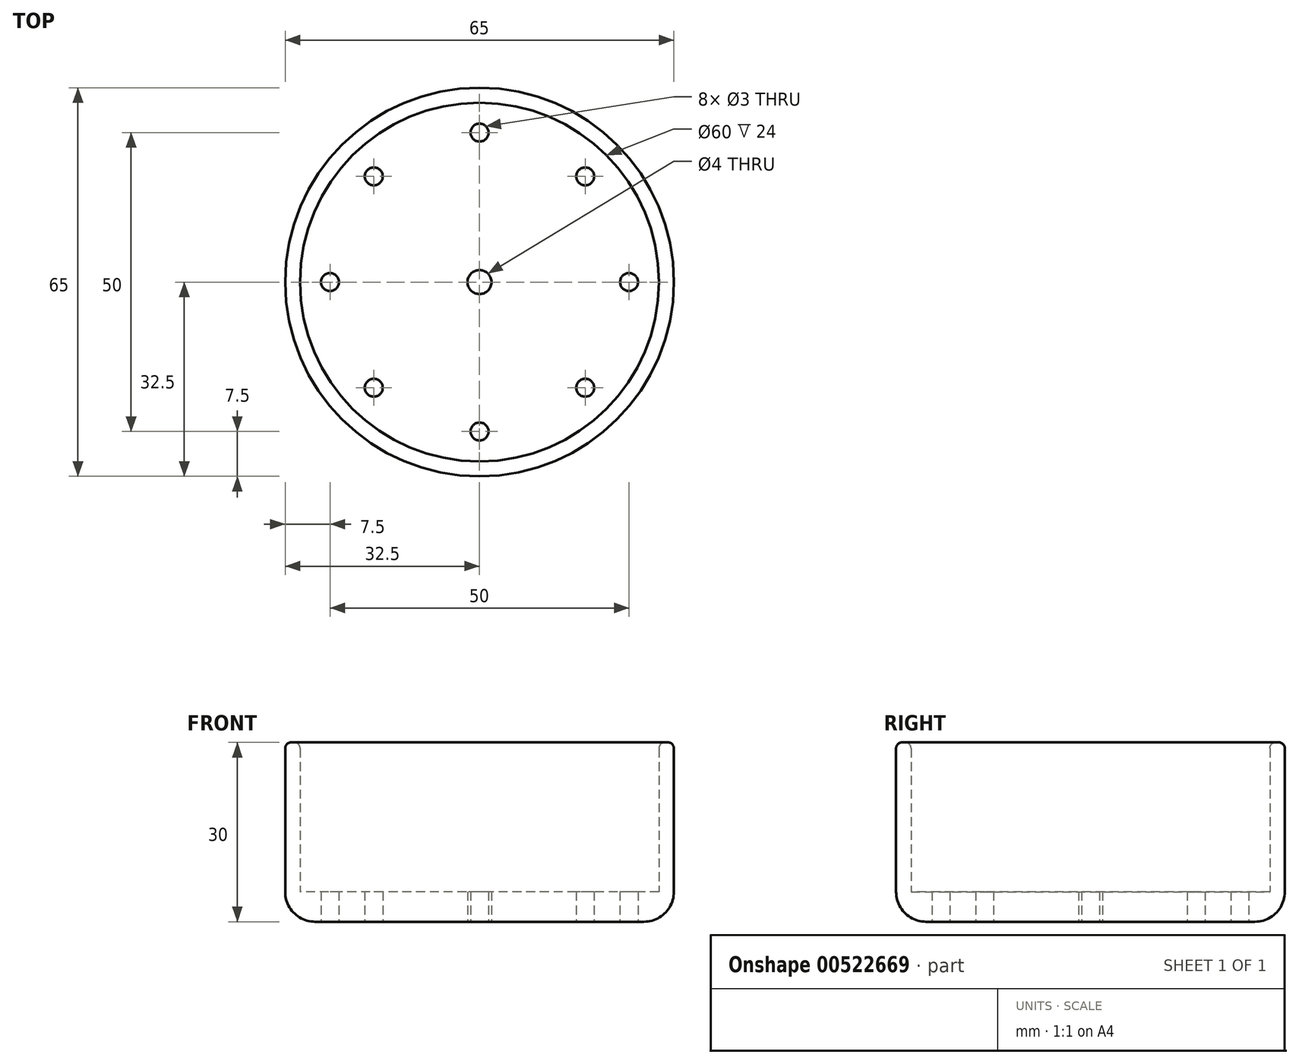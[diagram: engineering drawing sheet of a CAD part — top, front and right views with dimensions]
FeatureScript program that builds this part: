
annotation { "Feature Type Name" : "Feature", "Feature Type Description" : "" }
export const myFeature = defineFeature(function(context is Context, id is Id, definition is map)
    precondition{}
    {
        {
            var Q0;
            Q0=qCreatedBy(makeId("Top.planeOp"),FACE);
            var sketch = newSketch(context, id + "F0", { "sketchPlane" : qUnion([Q0])});
            skCircle(sketch, "E0", {"center": v(0, 0) * mm, "radius": 32.5 * mm});
            skSolve(sketch);
        }
        {
            var Q0;
            Q0 = qSketchRegion(id + "F0", true);
            extrude(context, id + "F1", {"entities" : qUnion([Q0]), "depth" : 5 * mm, "offsetDistance" : 25 * mm});
        }
        {
            var Q0;
            Q0=makeQuery(id+"F1.opExtrude","CAP_FACE",FACE,{"disambiguationData":[OSD([sQuery(id+"F0.wireOp",EDGE,"E0")])],"isStart":false});
            var sketch = newSketch(context, id + "F2", { "sketchPlane" : qUnion([Q0])});
            skCircle(sketch, "E1", {"center": v(0, 0) * mm, "radius": 30 * mm});
            skCircle(sketch, "E2.0", {"center": v(0, 0) * mm, "radius": 32.5 * mm});
            skSolve(sketch);
        }
        {
            var Q0;
            Q0=makeQuery(id+"F2.imprint","IMPRINT",FACE,{"disambiguationData":[TD([[makeQuery(id+"F2.imprint","IMPRINT",EDGE,{"derivedFrom":sQuery(id+"F2.wireOp",EDGE,"E1")}),-1.0]])]});
            extrude(context, id + "F3", {"entities" : qUnion([Q0]), "operationType" : NewBodyOperationType.ADD, "depth" : 25 * mm, "offsetDistance" : 25 * mm});
        }
        {
            var Q0;
            Q0=makeQuery(id+"F1.opExtrude","CAP_FACE",FACE,{"disambiguationData":[OSD([sQuery(id+"F0.wireOp",EDGE,"E0")])],"isStart":true});
            var sketch = newSketch(context, id + "F4", { "sketchPlane" : qUnion([Q0])});
            skCircle(sketch, "E3", {"center": v(0, 0) * mm, "radius": 2 * mm});
            skSolve(sketch);
        }
        {
            var Q0;
            Q0 = qSketchRegion(id + "F4", true);
            extrude(context, id + "F5", {"entities" : qUnion([Q0]), "operationType" : NewBodyOperationType.REMOVE, "oppositeDirection" : true, "depth" : 25 * mm, "offsetDistance" : 25 * mm});
        }
        {
            var Q0;
            Q0=makeQuery(id+"F1.opExtrude","CAP_FACE",FACE,{"disambiguationData":[OSD([sQuery(id+"F0.wireOp",EDGE,"E0")])],"isStart":true});
            var sketch = newSketch(context, id + "F6", { "sketchPlane" : qUnion([Q0])});
            skCircle(sketch, "E4", {"center": v(25, 0) * mm, "radius": 1.5 * mm});
            skLineSegment(sketch, "E5", {"start": v(0, 0) * mm, "end": v(25, 0) * mm});
            skCircle(sketch, "E6", {"center": v(17.68, 17.68) * mm, "radius": 1.5 * mm});
            skCircle(sketch, "E7", {"center": v(0, 25) * mm, "radius": 1.5 * mm});
            skLineSegment(sketch, "E8", {"start": v(0, 0) * mm, "end": v(-25, 0) * mm});
            skCircle(sketch, "E9", {"center": v(-17.68, 17.68) * mm, "radius": 1.5 * mm});
            skCircle(sketch, "E10", {"center": v(-25, 0) * mm, "radius": 1.5 * mm});
            skCircle(sketch, "E11", {"center": v(-17.68, -17.68) * mm, "radius": 1.5 * mm});
            skCircle(sketch, "E12", {"center": v(0, -25) * mm, "radius": 1.5 * mm});
            skCircle(sketch, "E13", {"center": v(17.68, -17.68) * mm, "radius": 1.5 * mm});
            skSolve(sketch);
        }
        {
            var Q0;
            Q0=makeQuery(id+"F6.imprint","IMPRINT",FACE,{"disambiguationData":[TD([[makeQuery(id+"F6.imprint","IMPRINT",EDGE,{"derivedFrom":sQuery(id+"F6.wireOp",EDGE,"E7")}),1.0]])]});
            var Q1;
            Q1=makeQuery(id+"F6.imprint","IMPRINT",FACE,{"disambiguationData":[TD([[makeQuery(id+"F6.imprint","IMPRINT",EDGE,{"derivedFrom":sQuery(id+"F6.wireOp",EDGE,"E6")}),1.0]])]});
            var Q2;
            Q2=makeQuery(id+"F6.imprint","IMPRINT",FACE,{"disambiguationData":[TD([[makeQuery(id+"F6.imprint","IMPRINT",EDGE,{"derivedFrom":sQuery(id+"F6.wireOp",EDGE,"E4")}),1.0]])]});
            var Q3;
            Q3=makeQuery(id+"F6.imprint","IMPRINT",FACE,{"disambiguationData":[TD([[makeQuery(id+"F6.imprint","IMPRINT",EDGE,{"derivedFrom":sQuery(id+"F6.wireOp",EDGE,"E13")}),1.0]])]});
            var Q4;
            Q4=makeQuery(id+"F6.imprint","IMPRINT",FACE,{"disambiguationData":[TD([[makeQuery(id+"F6.imprint","IMPRINT",EDGE,{"derivedFrom":sQuery(id+"F6.wireOp",EDGE,"E12")}),1.0]])]});
            var Q5;
            Q5=makeQuery(id+"F6.imprint","IMPRINT",FACE,{"disambiguationData":[TD([[makeQuery(id+"F6.imprint","IMPRINT",EDGE,{"derivedFrom":sQuery(id+"F6.wireOp",EDGE,"E11")}),1.0]])]});
            var Q6;
            Q6=makeQuery(id+"F6.imprint","IMPRINT",FACE,{"disambiguationData":[TD([[makeQuery(id+"F6.imprint","IMPRINT",EDGE,{"derivedFrom":sQuery(id+"F6.wireOp",EDGE,"E9")}),1.0]])]});
            var Q7;
            Q7=makeQuery(id+"F6.imprint","IMPRINT",FACE,{"disambiguationData":[TD([[makeQuery(id+"F6.imprint","IMPRINT",EDGE,{"derivedFrom":sQuery(id+"F6.wireOp",EDGE,"E10")}),1.0]])]});
            extrude(context, id + "F7", {"entities" : qUnion([Q0, Q1, Q2, Q3, Q4, Q5, Q6, Q7]), "operationType" : NewBodyOperationType.REMOVE, "oppositeDirection" : true, "depth" : 25 * mm, "offsetDistance" : 25 * mm});
        }
        {
            var Q0;
            Q0=makeQuery(id+"F1.opExtrude","CAP_EDGE",EDGE,{"disambiguationData":[OSD([sQuery(id+"F0.wireOp",EDGE,"E0")])],"isStart":true});
            fillet(context, id + "F8", {"entities" : qUnion([Q0]), "radius" : 5 * mm, "tangentPropagation" : true, "allowEdgeOverflow" : false});
        }
        {
            var Q0;
            Q0=makeQuery(id+"F3.opExtrude","CAP_EDGE",EDGE,{"disambiguationData":[OSD([sQuery(id+"F2.wireOp",EDGE,"E1")])],"isStart":false});
            var Q1;
            Q1=makeQuery(id+"F3.opExtrude","CAP_EDGE",EDGE,{"disambiguationData":[OSD([sQuery(id+"F2.wireOp",EDGE,"E2.0")])],"isStart":false});
            fillet(context, id + "F9", {"entities" : qUnion([Q0, Q1]), "radius" : 1 * mm, "tangentPropagation" : true, "allowEdgeOverflow" : false});
        }
    });
